# Revit family: KR6060001_Cepillera Koral
name_source: partatom
category: Furniture
units: mm (PartAtom-declared; Revit-internal decimal feet)

## family parameters
Always vertical = Yes
Cut with Voids When Loaded = No
Host = Wall
OmniClass Number = 23.31.25.00
OmniClass Title = Toilet and Bath Specialties
Room Calculation Point = No
Shared = No

## types (1)
- Type 1
    Colección = Koral
    Creado por = BIMBAU
    Default Elevation = 0 mm  [stored 0 ft]
    Description = Ofrécele a tu baño funcionalidad y elegancia con la cepillera Koral, con sistema de fijación oculto ¡Cómpralo ahora!
    Fecha de creación = 08/04/2021
    Garantía = 30 años en estructura
    Garantía Acabados = 3 años en acabado
    Manufacturer = Corona
    Material = Corona_Cromado
    Referencia = KR6060001
    URL = https://corona.co

note: [stored X ft] marks values corroborated as IEEE doubles in the binary element streams (Revit-internal decimal feet)

## geometry (parser evidence)
native form markers: Sweep x6
no freeform markers — native parametric forms only
